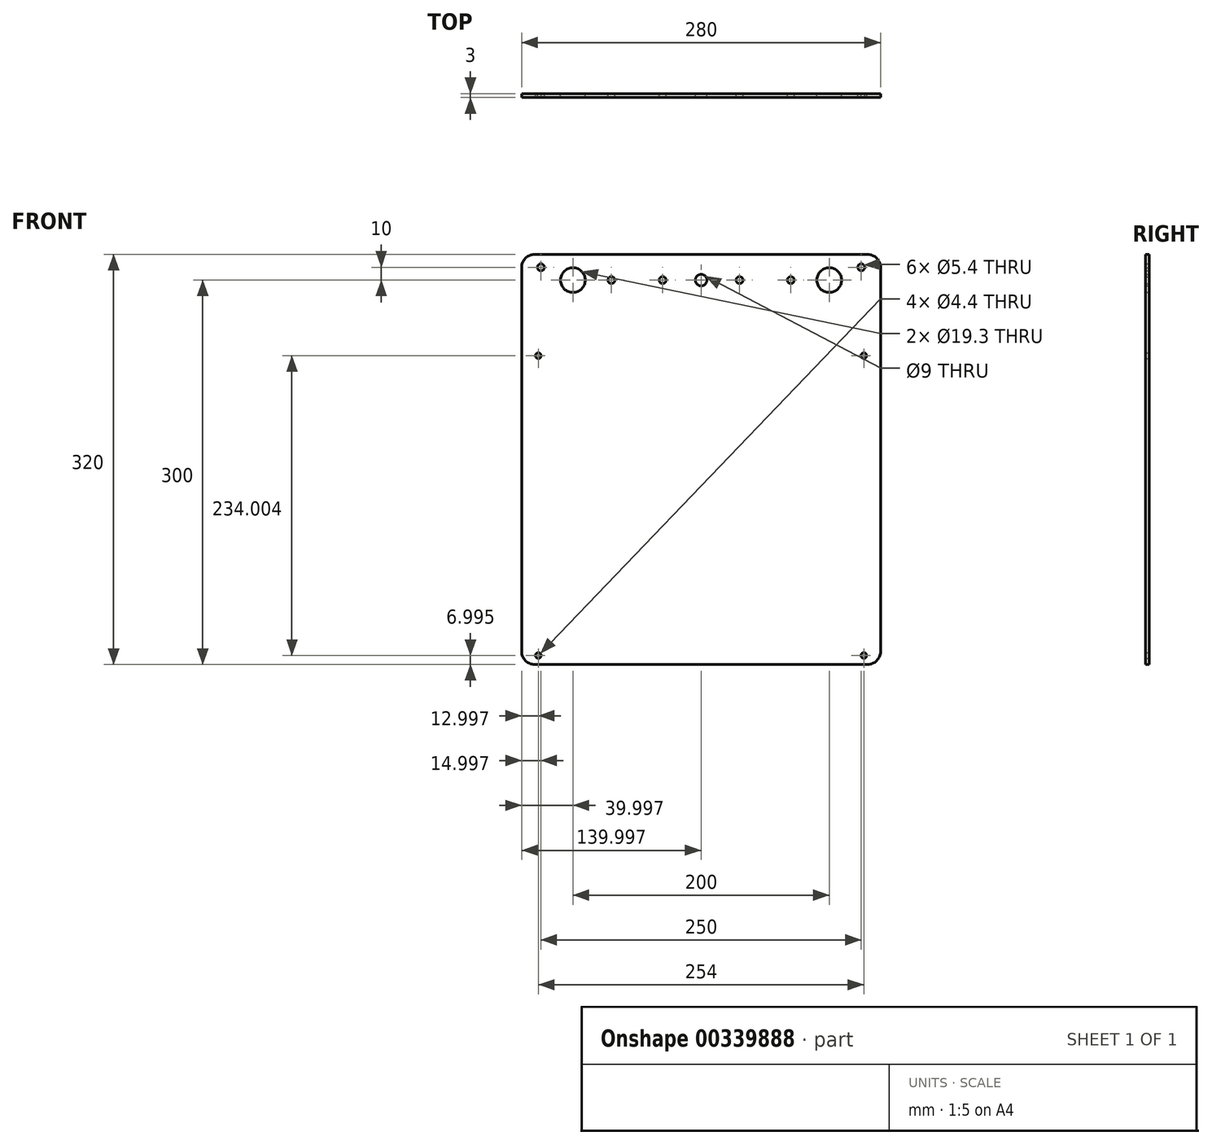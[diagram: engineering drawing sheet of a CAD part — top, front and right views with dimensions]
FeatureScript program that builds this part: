
annotation { "Feature Type Name" : "Feature", "Feature Type Description" : "" }
export const myFeature = defineFeature(function(context is Context, id is Id, definition is map)
    precondition{}
    {
        {
            var Q0;
            Q0=qCreatedBy(makeId("Front.planeOp"),FACE);
            var sketch = newSketch(context, id + "F0", { "sketchPlane" : qUnion([Q0])});
            skLineSegment(sketch, "E0.bottom", {"start": v(-124.2, 68.74) * mm, "end": v(155.8, 68.74) * mm});
            skLineSegment(sketch, "E0.top", {"start": v(-124.2, -251.26) * mm, "end": v(155.8, -251.26) * mm});
            skLineSegment(sketch, "E0.left", {"start": v(-124.2, 68.74) * mm, "end": v(-124.2, -251.26) * mm});
            skLineSegment(sketch, "E0.right", {"start": v(155.8, 68.74) * mm, "end": v(155.8, -251.26) * mm});
            skLineSegment(sketch, "E1", {"start": v(-124.2, 48.74) * mm, "end": v(155.8, 48.74) * mm, "construction": true});
            skCircle(sketch, "E2", {"center": v(15.8, 48.74) * mm, "radius": 4.5 * mm});
            skCircle(sketch, "E3", {"center": v(-84.2, 48.74) * mm, "radius": 9.65 * mm});
            skCircle(sketch, "E4", {"center": v(115.8, 48.74) * mm, "radius": 9.65 * mm});
            skCircle(sketch, "E5", {"center": v(-14.2, 48.74) * mm, "radius": 2.7 * mm});
            skCircle(sketch, "E6", {"center": v(-54.2, 48.74) * mm, "radius": 2.7 * mm});
            skCircle(sketch, "E7", {"center": v(45.8, 48.74) * mm, "radius": 2.7 * mm});
            skCircle(sketch, "E8", {"center": v(85.8, 48.74) * mm, "radius": 2.7 * mm});
            skLineSegment(sketch, "E9.bottom", {"start": v(-91.2, -20.26) * mm, "end": v(122.8, -20.26) * mm, "construction": true});
            skLineSegment(sketch, "E9.top", {"start": v(-91.2, -234.26) * mm, "end": v(122.8, -234.26) * mm, "construction": true});
            skLineSegment(sketch, "E9.left", {"start": v(-91.2, -20.26) * mm, "end": v(-91.2, -234.26) * mm, "construction": true});
            skLineSegment(sketch, "E9.right", {"start": v(122.8, -20.26) * mm, "end": v(122.8, -234.26) * mm, "construction": true});
            skCircle(sketch, "E10", {"center": v(-111.2, -10.26) * mm, "radius": 2.2 * mm});
            skCircle(sketch, "E11", {"center": v(-111.2, -244.26) * mm, "radius": 2.2 * mm});
            skCircle(sketch, "E12", {"center": v(142.8, -244.26) * mm, "radius": 2.2 * mm});
            skCircle(sketch, "E13", {"center": v(142.8, -10.26) * mm, "radius": 2.2 * mm});
            skCircle(sketch, "E14", {"center": v(-109.2, 58.74) * mm, "radius": 2.7 * mm});
            skCircle(sketch, "E15", {"center": v(140.8, 58.74) * mm, "radius": 2.7 * mm});
            skLineSegment(sketch, "E16.bottom", {"start": v(-111.2, -10.26) * mm, "end": v(142.8, -10.26) * mm, "construction": true});
            skLineSegment(sketch, "E16.top", {"start": v(-111.2, -244.26) * mm, "end": v(142.8, -244.26) * mm, "construction": true});
            skLineSegment(sketch, "E16.left", {"start": v(-111.2, -10.26) * mm, "end": v(-111.2, -244.26) * mm, "construction": true});
            skLineSegment(sketch, "E16.right", {"start": v(142.8, -10.26) * mm, "end": v(142.8, -244.26) * mm, "construction": true});
            skSolve(sketch);
        }
        {
            var Q0;
            Q0=makeQuery(id+"F0.imprint","IMPRINT",FACE,{"disambiguationData":[TD([[makeQuery(id+"F0.imprint","IMPRINT",EDGE,{"derivedFrom":sQuery(id+"F0.wireOp",EDGE,"E0.bottom")}),-1.0]])]});
            extrude(context, id + "F1", {"entities" : qUnion([Q0]), "depth" : 3 * mm});
        }
        {
            var Q0;
            Q0=makeQuery(id+"F1.opExtrude","SWEPT_EDGE",EDGE,{"disambiguationData":[OSD([sQuery(id+"F0.wireOp",EDGE,"E0.bottom"),sQuery(id+"F0.wireOp",EDGE,"E0.left")])]});
            var Q1;
            Q1=makeQuery(id+"F1.opExtrude","SWEPT_EDGE",EDGE,{"disambiguationData":[OSD([sQuery(id+"F0.wireOp",EDGE,"E0.bottom"),sQuery(id+"F0.wireOp",EDGE,"E0.right")])]});
            var Q2;
            Q2=makeQuery(id+"F1.opExtrude","SWEPT_EDGE",EDGE,{"disambiguationData":[OSD([sQuery(id+"F0.wireOp",EDGE,"E0.top"),sQuery(id+"F0.wireOp",EDGE,"E0.right")])]});
            var Q3;
            Q3=makeQuery(id+"F1.opExtrude","SWEPT_EDGE",EDGE,{"disambiguationData":[OSD([sQuery(id+"F0.wireOp",EDGE,"E0.top"),sQuery(id+"F0.wireOp",EDGE,"E0.left")])]});
            fillet(context, id + "F2", {"entities" : qUnion([Q0, Q1, Q2, Q3]), "radius" : 10 * mm, "tangentPropagation" : true, "allowEdgeOverflow" : false});
        }
    });
